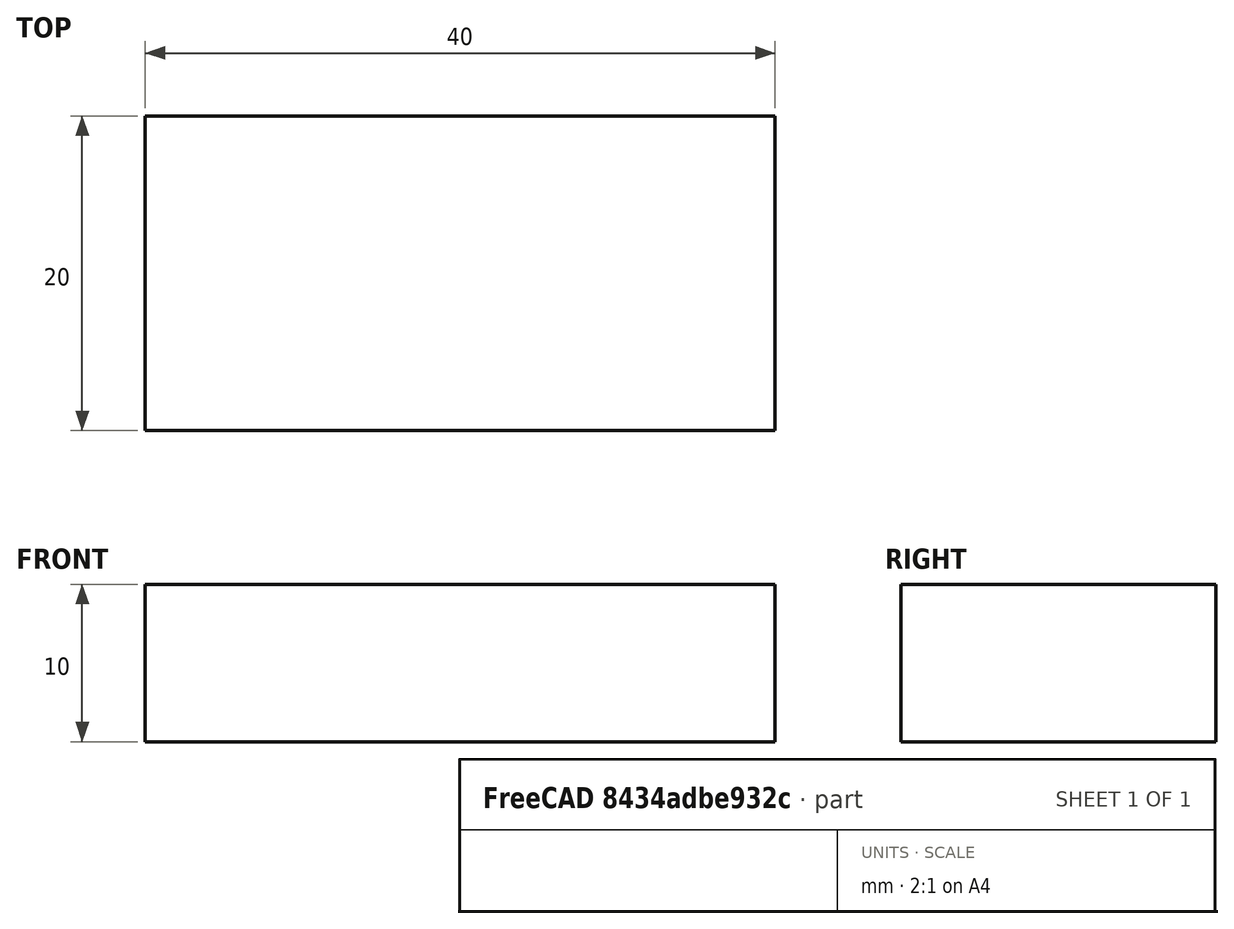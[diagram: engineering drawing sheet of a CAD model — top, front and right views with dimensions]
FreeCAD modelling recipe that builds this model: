
FCSTD DOCUMENT  (FreeCAD 1.0R38806 (Git))
Label: rectangulo
License: All rights reserved
LicenseURL: https://en.wikipedia.org/wiki/All_rights_reserved
objects: Sketcher::SketchObject×1, Part::Extrusion×1
note: 3 computed .brp shape members not serialized (recipe doc carries the construction recipe); baked Part::Feature solids carry a one-line shape summary decoded from their .brp

FEATURE [Sketcher::SketchObject] Sketch
  ArcFitTolerance = 1e-06
  FullyConstrained = true
  MakeInternals = false
  sketch-geometry (4):
    g0: LineSegment StartX=40 StartY=0 StartZ=0 EndX=40 EndY=20 EndZ=0
    g1: LineSegment StartX=0 StartY=0 StartZ=0 EndX=40 EndY=0 EndZ=0
    g2: LineSegment StartX=0 StartY=20 StartZ=0 EndX=40 EndY=20 EndZ=0
    g3: LineSegment StartX=0 StartY=20 StartZ=0 EndX=0 EndY=0 EndZ=0
  constraints (11):
    c: Coincident(g3,g2)
    c: Coincident(g2,g0)
    c: Coincident(g3,g1)
    c: Coincident(g0,g1)
    c: Horizontal(g2)
    c: Vertical(g3)
    c: Horizontal(g1)
    c: Vertical(g0)
    c: Coincident(g1,g-1)
    c: DistanceX(g2,g2) = 40  'ancho'
    c: Distance(g0,g0) = 20  'alto'
FEATURE [Part::Extrusion] Extrude  label="rectagulo"
  Base = -> Sketch
  Dir = (0,0,1)
  DirMode = 2
  FaceMakerClass = Part::FaceMakerBullseye
  FaceMakerMode = 3
  LengthFwd = 10
  LengthRev = 0
  Solid = true
  Symmetric = false
